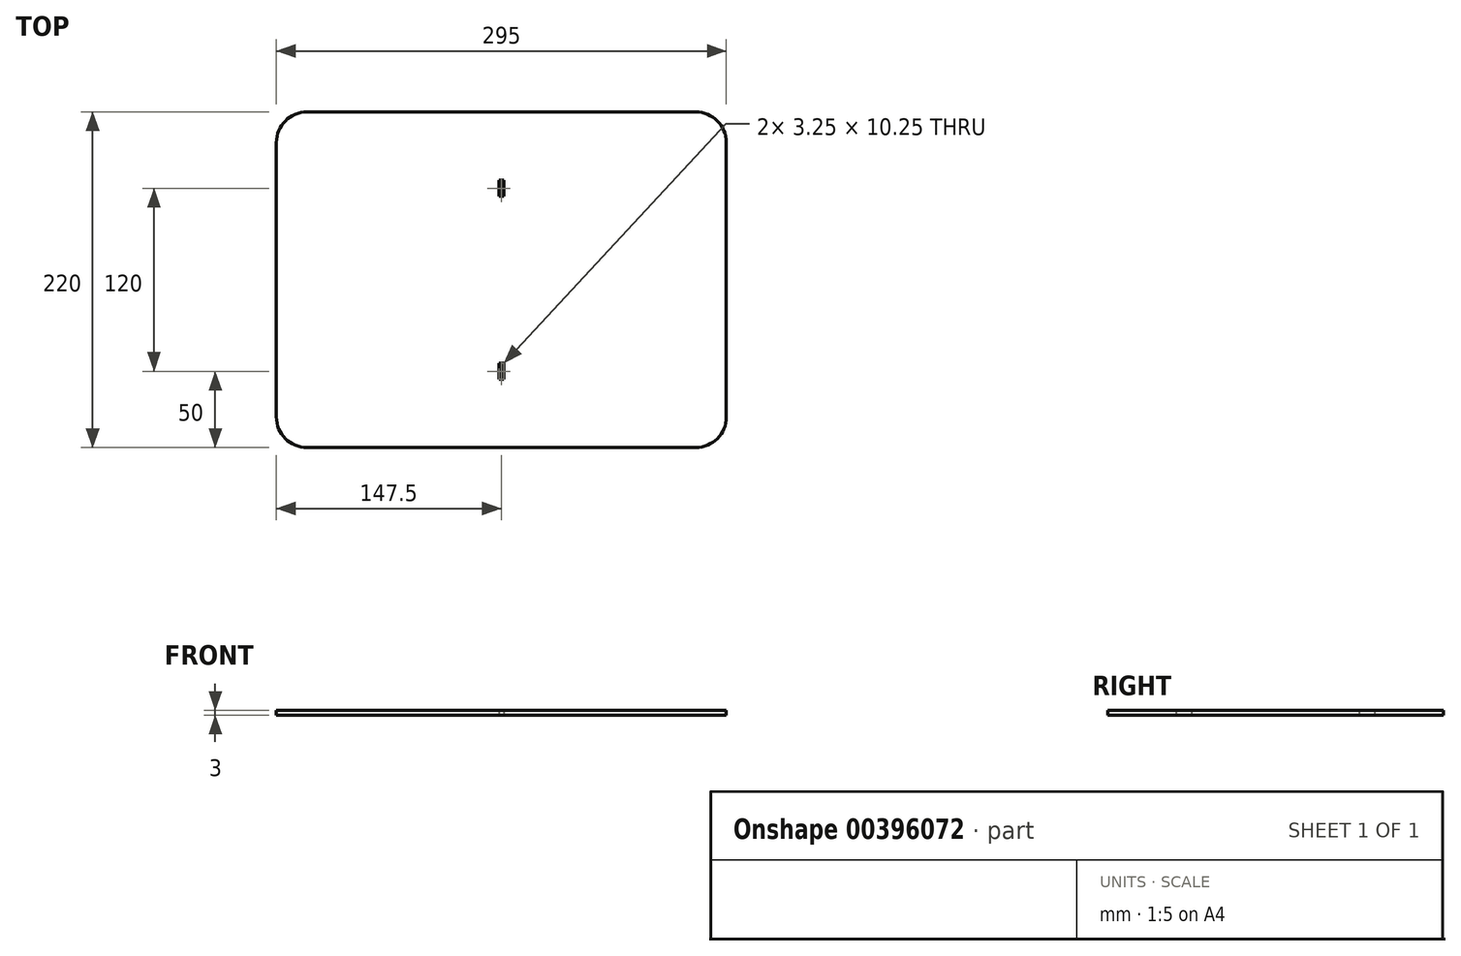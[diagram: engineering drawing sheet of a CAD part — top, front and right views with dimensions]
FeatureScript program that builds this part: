
annotation { "Feature Type Name" : "Feature", "Feature Type Description" : "" }
export const myFeature = defineFeature(function(context is Context, id is Id, definition is map)
    precondition{}
    {
        {
            var Q0;
            Q0=qCreatedBy(makeId("Top.planeOp"),FACE);
            var sketch = newSketch(context, id + "F0", { "sketchPlane" : qUnion([Q0])});
            skLineSegment(sketch, "E0.bottom", {"start": v(-127.5, 110) * mm, "end": v(127.5, 110) * mm});
            skLineSegment(sketch, "E0.top", {"start": v(-127.5, -110) * mm, "end": v(127.5, -110) * mm});
            skLineSegment(sketch, "E0.left", {"start": v(-147.5, 90) * mm, "end": v(-147.5, -90) * mm});
            skLineSegment(sketch, "E0.right", {"start": v(147.5, 90) * mm, "end": v(147.5, -90) * mm});
            skPoint(sketch, "E0.middle", {"position": v(0, 0) * mm});
            skPoint(sketch, "E1.visualSharp", {"position": v(-147.5, 110) * mm});
            skArc(sketch, "E1.filletArc", {"start": v(-127.5, 110) * mm, "mid": v(-141.64, 104.14) * mm, "end": v(-147.5, 90) * mm});
            skPoint(sketch, "E2.visualSharp", {"position": v(-147.5, -110) * mm});
            skArc(sketch, "E2.filletArc", {"start": v(-147.5, -90) * mm, "mid": v(-141.64, -104.14) * mm, "end": v(-127.5, -110) * mm});
            skPoint(sketch, "E3.visualSharp", {"position": v(147.5, -110) * mm});
            skArc(sketch, "E3.filletArc", {"start": v(127.5, -110) * mm, "mid": v(141.64, -104.14) * mm, "end": v(147.5, -90) * mm});
            skPoint(sketch, "E4.visualSharp", {"position": v(147.5, 110) * mm});
            skArc(sketch, "E4.filletArc", {"start": v(147.5, 90) * mm, "mid": v(141.64, 104.14) * mm, "end": v(127.5, 110) * mm});
            skPoint(sketch, "E5.bottom.start.orphan", {"position": v(-125, 85) * mm});
            skPoint(sketch, "E5.right.start.orphan", {"position": v(125, 85) * mm});
            skPoint(sketch, "E5.top.end.orphan", {"position": v(125, -85) * mm});
            skPoint(sketch, "E5.top.start.orphan", {"position": v(-125, -85) * mm});
            skLineSegment(sketch, "E6", {"start": v(0, 110) * mm, "end": v(0, -110) * mm, "construction": true});
            skLineSegment(sketch, "E7", {"start": v(-147.5, 0) * mm, "end": v(147.5, 0) * mm, "construction": true});
            skLineSegment(sketch, "E8.bottom", {"start": v(-1.62, 65.13) * mm, "end": v(1.63, 65.13) * mm});
            skLineSegment(sketch, "E8.top", {"start": v(-1.62, 54.88) * mm, "end": v(1.63, 54.88) * mm});
            skLineSegment(sketch, "E8.left", {"start": v(-1.62, 65.13) * mm, "end": v(-1.62, 54.88) * mm});
            skLineSegment(sketch, "E8.right", {"start": v(1.63, 65.13) * mm, "end": v(1.63, 54.88) * mm});
            skPoint(sketch, "E8.middle", {"position": v(0, 60) * mm});
            skLineSegment(sketch, "E9.MirrorCS", {"start": v(1.63, -65.13) * mm, "end": v(1.63, -54.88) * mm});
            skLineSegment(sketch, "E10.MirrorCS", {"start": v(-1.62, -65.13) * mm, "end": v(-1.62, -54.88) * mm});
            skLineSegment(sketch, "E11.MirrorCS", {"start": v(-1.62, -65.12) * mm, "end": v(1.63, -65.12) * mm});
            skLineSegment(sketch, "E12.MirrorCS", {"start": v(-1.62, -54.88) * mm, "end": v(1.63, -54.88) * mm});
            skSolve(sketch);
        }
        {
            var Q0;
            Q0=qSketchRegion(id+"F0",true);
            extrude(context, id + "F1", {"entities" : qUnion([Q0]), "depth" : 3 * mm});
        }
    });
